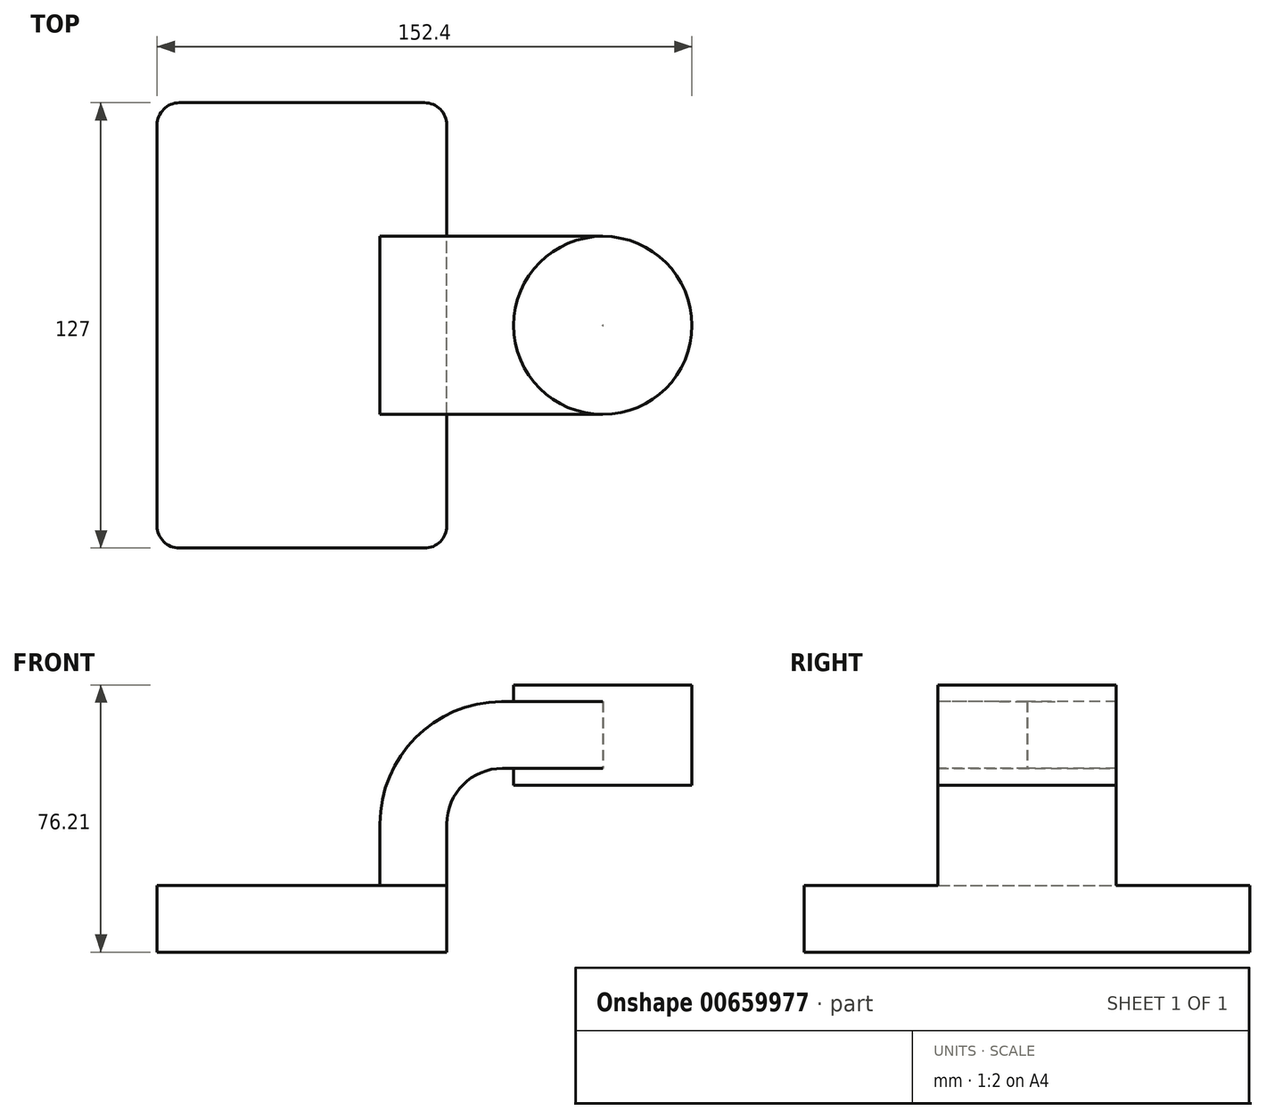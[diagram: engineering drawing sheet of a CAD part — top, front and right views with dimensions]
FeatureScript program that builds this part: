
annotation { "Feature Type Name" : "Feature", "Feature Type Description" : "" }
export const myFeature = defineFeature(function(context is Context, id is Id, definition is map)
    precondition{}
    {
        {
            var Q0;
            Q0=qCreatedBy(makeId("Front.planeOp"),FACE);
            var sketch = newSketch(context, id + "F0", { "sketchPlane" : qUnion([Q0])});
            skLineSegment(sketch, "E0.bottom", {"start": v(-41.27, -9.53) * mm, "end": v(41.28, -9.53) * mm});
            skLineSegment(sketch, "E0.top", {"start": v(-41.28, 9.52) * mm, "end": v(41.28, 9.52) * mm});
            skLineSegment(sketch, "E0.left", {"start": v(-41.28, -9.53) * mm, "end": v(-41.28, 9.53) * mm});
            skLineSegment(sketch, "E0.right", {"start": v(41.28, -9.53) * mm, "end": v(41.28, 9.52) * mm});
            skPoint(sketch, "E0.middle", {"position": v(0, 0) * mm});
            skLineSegment(sketch, "E1.bottom", {"start": v(60.33, 38.1) * mm, "end": v(111.12, 38.1) * mm});
            skLineSegment(sketch, "E1.top", {"start": v(60.33, 66.67) * mm, "end": v(111.12, 66.67) * mm});
            skLineSegment(sketch, "E1.left", {"start": v(60.33, 38.1) * mm, "end": v(60.33, 66.67) * mm});
            skLineSegment(sketch, "E1.right", {"start": v(111.12, 38.1) * mm, "end": v(111.12, 66.67) * mm});
            skPoint(sketch, "E1.middle", {"position": v(85.72, 52.39) * mm});
            skLineSegment(sketch, "E2", {"start": v(41.28, 9.52) * mm, "end": v(41.28, 27) * mm});
            skArc(sketch, "E3", {"start": v(41.27, 27) * mm, "mid": v(45.92, 38.23) * mm, "end": v(57.15, 42.88) * mm});
            skLineSegment(sketch, "E4", {"start": v(57.15, 42.88) * mm, "end": v(85.8, 42.88) * mm});
            skLineSegment(sketch, "E5.0", {"start": v(57.15, 61.93) * mm, "end": v(85.8, 61.93) * mm});
            skArc(sketch, "E5.1", {"start": v(22.22, 27) * mm, "mid": v(32.45, 51.7) * mm, "end": v(57.15, 61.93) * mm});
            skLineSegment(sketch, "E5.2", {"start": v(22.22, 9.52) * mm, "end": v(22.22, 27) * mm});
            skLineSegment(sketch, "E6", {"start": v(85.8, 61.93) * mm, "end": v(85.8, 42.88) * mm});
            skFitSpline(sketch, "E7", {"points": [v(-41.28, 9.53) * mm, v(57.15, 61.93) * mm], "startDerivative": vector(0.4, 74.03) * mm, "endDerivative": vector(141.74, 0.48) * mm});
            skLineSegment(sketch, "E8", {"start": v(85.72, 38.1) * mm, "end": v(85.72, 66.67) * mm});
            skSolve(sketch);
        }
        {
            var Q0;
            Q0=makeQuery(id+"F0.imprint","IMPRINT",FACE,{"disambiguationData":[TD([[makeQuery(id+"F0.imprint","IMPRINT",EDGE,{"derivedFrom":sQuery(id+"F0.wireOp",EDGE,"E0.bottom")}),1.0]])]});
            extrude(context, id + "F1", {"entities" : qUnion([Q0]), "endBound" : BoundingType.SYMMETRIC, "depth" : 127 * mm, "offsetDistance" : 25.4 * mm});
        }
        {
            var Q0;
            {var subQ4=sQuery(id+"F0.wireOp",EDGE,"E5.1");Q0=makeQuery(id+"F0.imprint","IMPRINT",FACE,{"disambiguationData":[TD([[makeQuery(id+"F0.imprint","IMPRINT",EDGE,{"derivedFrom":subQ4}),1.0]])]});}
            extrude(context, id + "F2", {"entities" : qUnion([Q0]), "operationType" : NewBodyOperationType.ADD, "endBound" : BoundingType.SYMMETRIC, "depth" : 15.88 * mm, "offsetDistance" : 25.4 * mm});
        }
        {
            var Q0;
            {var subQ5=sQuery(id+"F0.wireOp",EDGE,"E2");Q0=makeQuery(id+"F0.imprint","IMPRINT",FACE,{"disambiguationData":[TD([[makeQuery(id+"F0.imprint","IMPRINT",EDGE,{"derivedFrom":subQ5}),1.0]])]});}
            var Q1;
            {var subQ0=sQuery(id+"F0.wireOp",EDGE,"E4");var subQ1=sQuery(id+"F0.wireOp",EDGE,"E1.left");var subQ2=makeQuery(id+"F0.imprint","INTERSECT",VERTEX,{"derivedFrom":[subQ1,subQ0]});Q1=makeQuery(id+"F0.imprint","IMPRINT",FACE,{"disambiguationData":[TD([[makeQuery(id+"F0.imprint","IMPRINT",EDGE,{"disambiguationData":[TD([[subQ2,-1.0]])],"derivedFrom":subQ1}),-1.0]])]});}
            extrude(context, id + "F3", {"entities" : qUnion([Q0, Q1]), "operationType" : NewBodyOperationType.ADD, "endBound" : BoundingType.SYMMETRIC, "depth" : 50.8 * mm, "offsetDistance" : 25.4 * mm});
        }
        {
            var Q0;
            {var subQ4=sQuery(id+"F0.wireOp",EDGE,"E1.right");Q0=makeQuery(id+"F0.imprint","IMPRINT",FACE,{"disambiguationData":[TD([[makeQuery(id+"F0.imprint","IMPRINT",EDGE,{"derivedFrom":subQ4}),1.0]])]});}
            var Q1;
            Q1=sQuery(id+"F0.wireOp",EDGE,"E8");
            revolve(context, id + "F4", {"operationType" : NewBodyOperationType.ADD, "entities" : qUnion([Q0]), "axis" : qUnion([Q1]), "revolveType" : RevolveType.FULL});
        }
        {
            var Q0;
            Q0=makeQuery(id+"F1.opExtrude","CAP_EDGE",EDGE,{"disambiguationData":[OSD([sQuery(id+"F0.wireOp",EDGE,"E0.left")])],"isStart":false});
            var Q1;
            Q1=makeQuery(id+"F1.opExtrude","CAP_EDGE",EDGE,{"disambiguationData":[OSD([sQuery(id+"F0.wireOp",EDGE,"E0.right")])],"isStart":false});
            var Q2;
            Q2=makeQuery(id+"F1.opExtrude","CAP_EDGE",EDGE,{"disambiguationData":[OSD([sQuery(id+"F0.wireOp",EDGE,"E0.right")])],"isStart":true});
            var Q3;
            Q3=makeQuery(id+"F1.opExtrude","CAP_EDGE",EDGE,{"disambiguationData":[OSD([sQuery(id+"F0.wireOp",EDGE,"E0.left")])],"isStart":true});
            fillet(context, id + "F5", {"entities" : qUnion([Q0, Q1, Q2, Q3]), "radius" : 6.35 * mm, "tangentPropagation" : true, "allowEdgeOverflow" : false});
        }
    });
